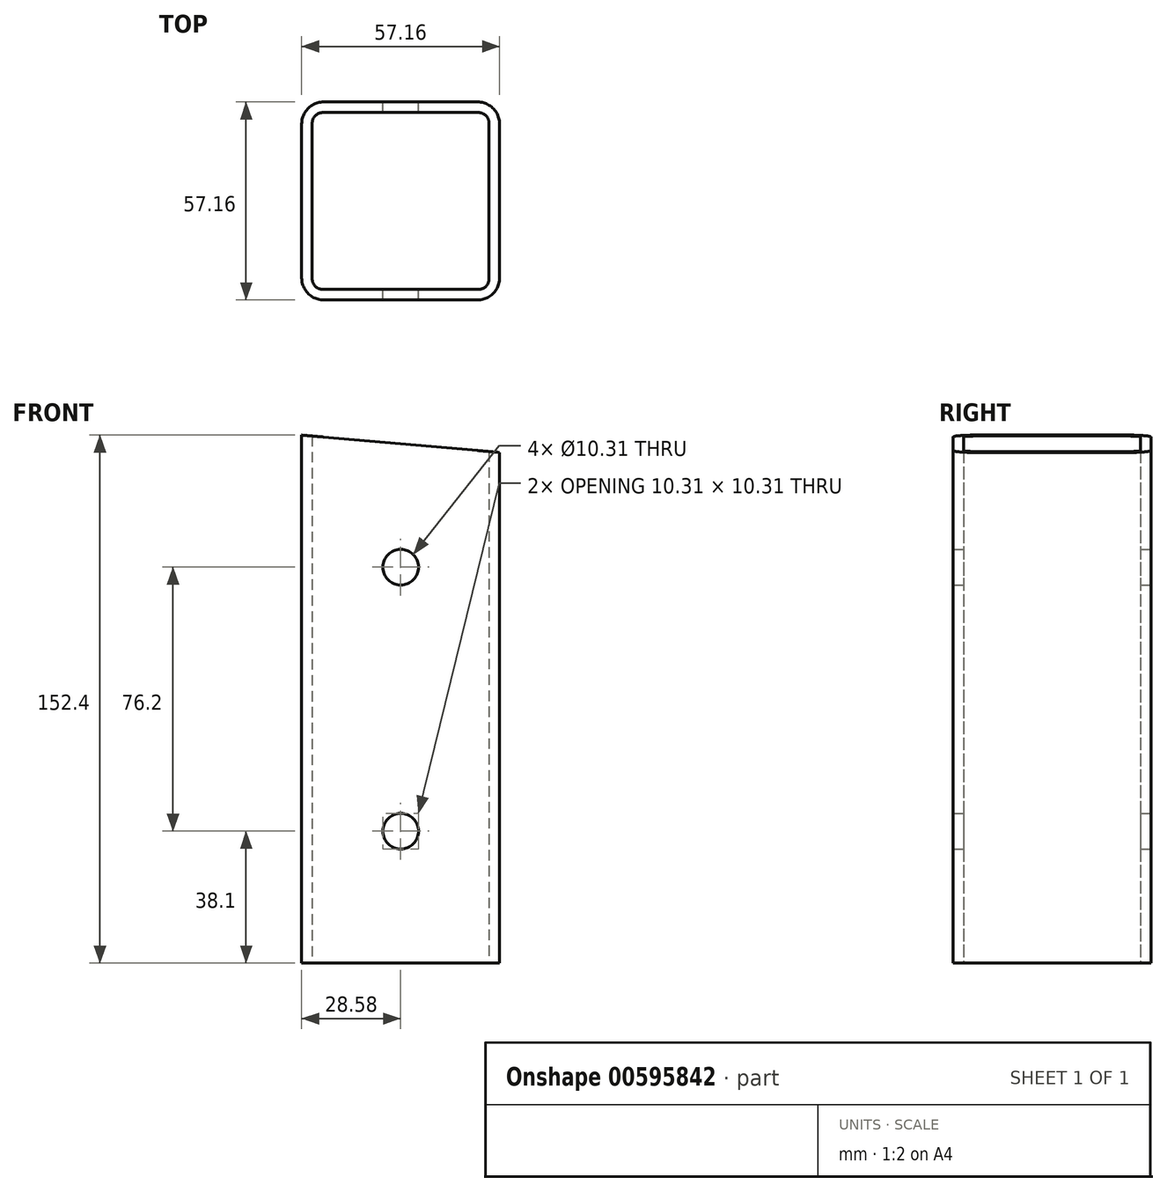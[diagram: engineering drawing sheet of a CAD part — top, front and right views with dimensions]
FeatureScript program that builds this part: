
annotation { "Feature Type Name" : "Feature", "Feature Type Description" : "" }
export const myFeature = defineFeature(function(context is Context, id is Id, definition is map)
    precondition{}
    {
        {
            var Q0;
            Q0=qCreatedBy(makeId("Top.planeOp"),FACE);
            var sketch = newSketch(context, id + "F0", { "sketchPlane" : qUnion([Q0])});
            skLineSegment(sketch, "E0.bottom", {"start": v(28.58, -28.58) * mm, "end": v(-28.58, -28.58) * mm});
            skLineSegment(sketch, "E0.top", {"start": v(28.58, 28.58) * mm, "end": v(-28.58, 28.58) * mm});
            skLineSegment(sketch, "E0.left", {"start": v(28.58, -28.58) * mm, "end": v(28.58, 28.58) * mm});
            skLineSegment(sketch, "E0.right", {"start": v(-28.57, -28.58) * mm, "end": v(-28.58, 28.58) * mm});
            skPoint(sketch, "E0.middle", {"position": v(0, 0) * mm});
            skLineSegment(sketch, "E1.bottom", {"start": v(-25.53, 25.53) * mm, "end": v(25.53, 25.53) * mm});
            skLineSegment(sketch, "E1.top", {"start": v(-25.53, -25.53) * mm, "end": v(25.53, -25.53) * mm});
            skLineSegment(sketch, "E1.left", {"start": v(-25.53, 25.53) * mm, "end": v(-25.53, -25.53) * mm});
            skLineSegment(sketch, "E1.right", {"start": v(25.53, 25.53) * mm, "end": v(25.53, -25.53) * mm});
            skSolve(sketch);
        }
        {
            var Q0;
            Q0 = qSketchRegion(id + "F0", true);
            extrude(context, id + "F1", {"entities" : qUnion([Q0]), "depth" : 152.4 * mm, "offsetDistance" : 25.4 * mm});
        }
        {
            var Q0;
            Q0=makeQuery(id+"F1.opExtrude","SWEPT_EDGE",EDGE,{"disambiguationData":[OSD([sQuery(id+"F0.wireOp",EDGE,"E1.bottom"),sQuery(id+"F0.wireOp",EDGE,"E1.right")])]});
            var Q1;
            Q1=makeQuery(id+"F1.opExtrude","SWEPT_EDGE",EDGE,{"disambiguationData":[OSD([sQuery(id+"F0.wireOp",EDGE,"E1.bottom"),sQuery(id+"F0.wireOp",EDGE,"E1.left")])]});
            var Q2;
            Q2=makeQuery(id+"F1.opExtrude","SWEPT_EDGE",EDGE,{"disambiguationData":[OSD([sQuery(id+"F0.wireOp",EDGE,"E1.top"),sQuery(id+"F0.wireOp",EDGE,"E1.left")])]});
            var Q3;
            Q3=makeQuery(id+"F1.opExtrude","SWEPT_EDGE",EDGE,{"disambiguationData":[OSD([sQuery(id+"F0.wireOp",EDGE,"E1.top"),sQuery(id+"F0.wireOp",EDGE,"E1.right")])]});
            fillet(context, id + "F2", {"entities" : qUnion([Q0, Q1, Q2, Q3]), "radius" : 3.05 * mm, "tangentPropagation" : true, "allowEdgeOverflow" : false});
        }
        {
            var Q0;
            Q0=makeQuery(id+"F1.opExtrude","SWEPT_EDGE",EDGE,{"disambiguationData":[OSD([sQuery(id+"F0.wireOp",EDGE,"E0.top"),sQuery(id+"F0.wireOp",EDGE,"E0.right")])]});
            var Q1;
            Q1=makeQuery(id+"F1.opExtrude","SWEPT_EDGE",EDGE,{"disambiguationData":[OSD([sQuery(id+"F0.wireOp",EDGE,"E0.bottom"),sQuery(id+"F0.wireOp",EDGE,"E0.right")])]});
            var Q2;
            Q2=makeQuery(id+"F1.opExtrude","SWEPT_EDGE",EDGE,{"disambiguationData":[OSD([sQuery(id+"F0.wireOp",EDGE,"E0.bottom"),sQuery(id+"F0.wireOp",EDGE,"E0.left")])]});
            var Q3;
            Q3=makeQuery(id+"F1.opExtrude","SWEPT_EDGE",EDGE,{"disambiguationData":[OSD([sQuery(id+"F0.wireOp",EDGE,"E0.top"),sQuery(id+"F0.wireOp",EDGE,"E0.left")])]});
            fillet(context, id + "F3", {"entities" : qUnion([Q0, Q1, Q2, Q3]), "radius" : 6.35 * mm, "tangentPropagation" : true, "allowEdgeOverflow" : false});
        }
        {
            var Q0;
            Q0=qCreatedBy(makeId("Front.planeOp"),FACE);
            var sketch = newSketch(context, id + "F4", { "sketchPlane" : qUnion([Q0])});
            skLineSegment(sketch, "E2", {"start": v(28.58, 147.4) * mm, "end": v(-28.58, 152.4) * mm});
            skLineSegment(sketch, "E3", {"start": v(-28.58, 152.4) * mm, "end": v(28.58, 152.4) * mm});
            skLineSegment(sketch, "E4", {"start": v(28.58, 152.4) * mm, "end": v(28.58, 147.4) * mm});
            skSolve(sketch);
        }
        {
            var Q0;
            Q0 = qSketchRegion(id + "F4", true);
            extrude(context, id + "F5", {"entities" : qUnion([Q0]), "operationType" : NewBodyOperationType.REMOVE, "endBound" : BoundingType.THROUGH_ALL, "oppositeDirection" : true, "depth" : 25.4 * mm, "offsetDistance" : 25.4 * mm, "hasSecondDirection" : true, "secondDirectionBound" : SecondDirectionBoundingType.THROUGH_ALL, "secondDirectionOppositeDirection" : false, "secondDirectionDepth" : 25.4 * mm});
        }
        {
            var Q0;
            Q0=qCreatedBy(makeId("Front.planeOp"),FACE);
            var sketch = newSketch(context, id + "F6", { "sketchPlane" : qUnion([Q0])});
            skCircle(sketch, "E5", {"center": v(0, 114.3) * mm, "radius": 5.16 * mm});
            skCircle(sketch, "E6", {"center": v(0, 38.1) * mm, "radius": 5.16 * mm});
            skSolve(sketch);
        }
        {
            var Q0;
            Q0 = qSketchRegion(id + "F6", true);
            extrude(context, id + "F7", {"entities" : qUnion([Q0]), "operationType" : NewBodyOperationType.REMOVE, "endBound" : BoundingType.THROUGH_ALL, "depth" : 25.4 * mm, "offsetDistance" : 25.4 * mm, "hasSecondDirection" : true, "secondDirectionBound" : SecondDirectionBoundingType.THROUGH_ALL, "secondDirectionOppositeDirection" : true, "secondDirectionDepth" : 25.4 * mm});
        }
    });
